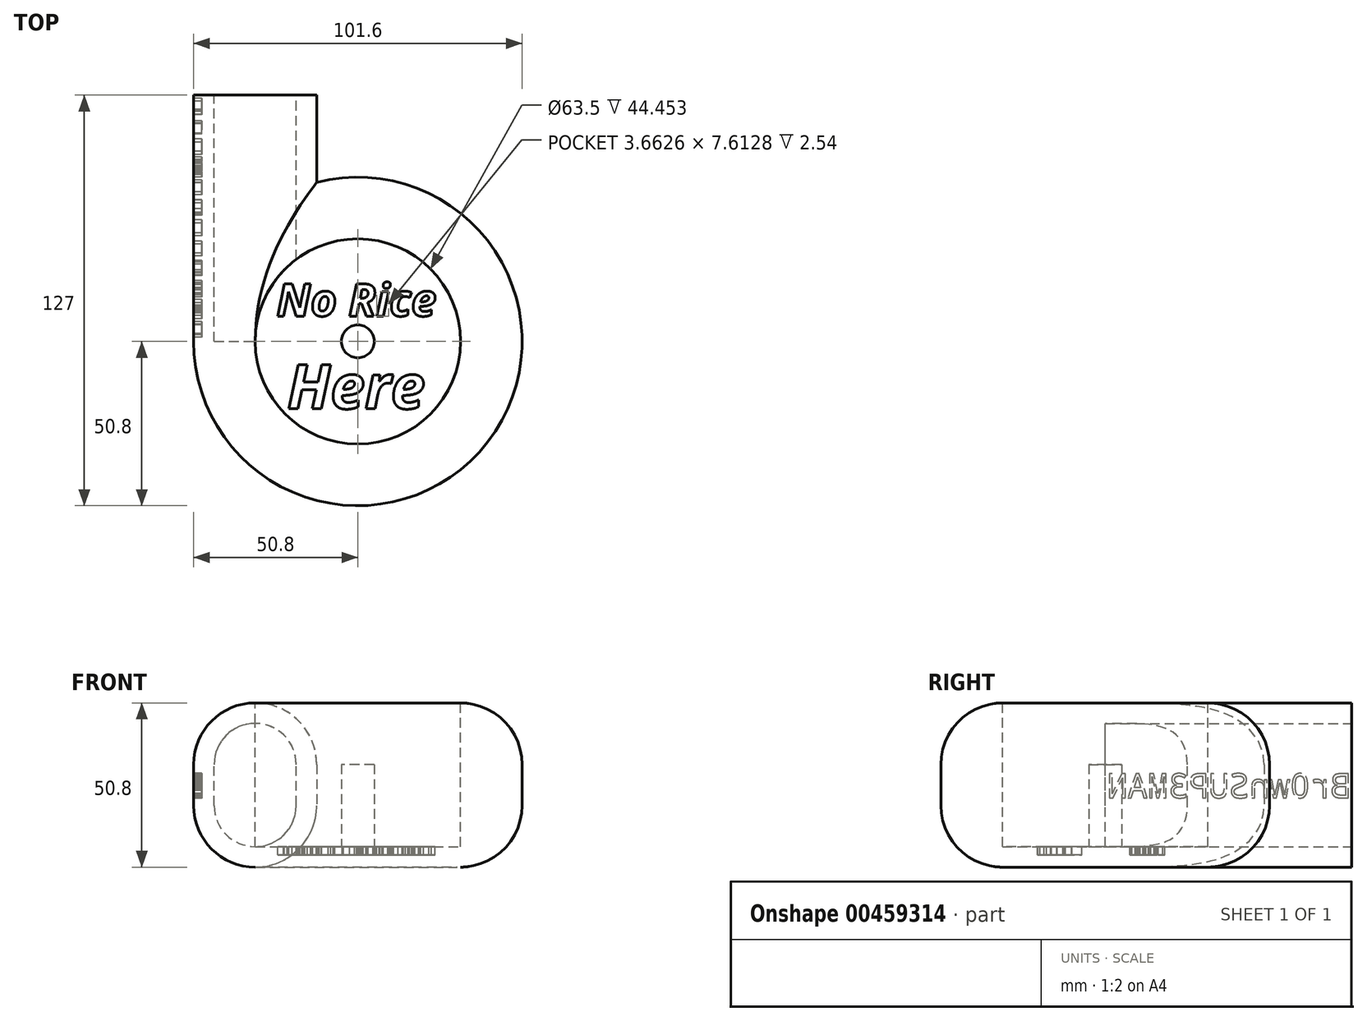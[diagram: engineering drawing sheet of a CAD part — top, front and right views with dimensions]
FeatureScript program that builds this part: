
annotation { "Feature Type Name" : "Feature", "Feature Type Description" : "" }
export const myFeature = defineFeature(function(context is Context, id is Id, definition is map)
    precondition{}
    {
        {
            var Q0;
            Q0=qCreatedBy(makeId("Top.planeOp"),FACE);
            var sketch = newSketch(context, id + "F0", { "sketchPlane" : qUnion([Q0])});
            skLineSegment(sketch, "E0", {"start": v(-50.8, 0) * mm, "end": v(-50.8, 76.2) * mm});
            skLineSegment(sketch, "E1", {"start": v(-50.8, 76.2) * mm, "end": v(-12.7, 76.2) * mm});
            skLineSegment(sketch, "E2", {"start": v(-12.7, 76.2) * mm, "end": v(-12.7, 49.19) * mm});
            skArc(sketch, "E3", {"start": v(-50.8, 0) * mm, "mid": v(40.16, -31.1) * mm, "end": v(-12.7, 49.19) * mm});
            skSolve(sketch);
        }
        {
            var Q0;
            Q0=makeQuery(id+"F0.imprint","IMPRINT",FACE,{"disambiguationData":[TD([[makeQuery(id+"F0.imprint","IMPRINT",EDGE,{"derivedFrom":sQuery(id+"F0.wireOp",EDGE,"E0")}),-1.0]])]});
            extrude(context, id + "F1", {"entities" : qUnion([Q0]), "depth" : 50.8 * mm});
        }
        {
            var Q0;
            Q0=makeQuery(id+"F1.opExtrude","CAP_EDGE",EDGE,{"disambiguationData":[OSD([sQuery(id+"F0.wireOp",EDGE,"E0")])],"isStart":false});
            var Q1;
            Q1=makeQuery(id+"F1.opExtrude","CAP_EDGE",EDGE,{"disambiguationData":[OSD([sQuery(id+"F0.wireOp",EDGE,"E2")])],"isStart":false});
            fillet(context, id + "F2", {"entities" : qUnion([Q0, Q1]), "radius" : 19.05 * mm, "tangentPropagation" : true, "allowEdgeOverflow" : false});
        }
        {
            var Q0;
            Q0=makeQuery(id+"F1.opExtrude","CAP_EDGE",EDGE,{"disambiguationData":[OSD([sQuery(id+"F0.wireOp",EDGE,"E0")])],"isStart":true});
            var Q1;
            Q1=makeQuery(id+"F1.opExtrude","CAP_EDGE",EDGE,{"disambiguationData":[OSD([sQuery(id+"F0.wireOp",EDGE,"E2")])],"isStart":true});
            fillet(context, id + "F3", {"entities" : qUnion([Q0, Q1]), "radius" : 19.05 * mm, "tangentPropagation" : true, "allowEdgeOverflow" : false});
        }
        {
            var Q0;
            Q0=makeQuery(id+"F1.opExtrude","SWEPT_FACE",FACE,{"disambiguationData":[OSD([sQuery(id+"F0.wireOp",EDGE,"E1")])]});
            var sketch = newSketch(context, id + "F4", { "sketchPlane" : qUnion([Q0])});
            skLineSegment(sketch, "E4", {"start": v(44.45, 6.35) * mm, "end": v(19.05, 6.35) * mm});
            skLineSegment(sketch, "E5", {"start": v(44.45, 44.45) * mm, "end": v(44.45, 44.45) * mm});
            skLineSegment(sketch, "E6", {"start": v(44.45, 6.35) * mm, "end": v(44.45, 44.45) * mm});
            skLineSegment(sketch, "E7", {"start": v(19.05, 6.35) * mm, "end": v(19.05, 6.35) * mm});
            skLineSegment(sketch, "E8", {"start": v(19.05, 6.35) * mm, "end": v(19.05, 44.45) * mm});
            skLineSegment(sketch, "E9", {"start": v(44.45, 44.45) * mm, "end": v(19.05, 44.45) * mm});
            skSolve(sketch);
        }
        {
            var Q0;
            Q0=makeQuery(id+"F4.imprint","IMPRINT",FACE,{"disambiguationData":[TD([[makeQuery(id+"F4.imprint","IMPRINT",EDGE,{"derivedFrom":sQuery(id+"F4.wireOp",EDGE,"E4")}),-1.0]])]});
            extrude(context, id + "F5", {"entities" : qUnion([Q0]), "operationType" : NewBodyOperationType.ADD, "depth" : 25.4 * mm});
        }
        {
            var Q0;
            Q0=makeQuery(id+"F5.opExtrude","SWEPT_EDGE",EDGE,{"disambiguationData":[OSD([sQuery(id+"F4.wireOp",EDGE,"E4"),sQuery(id+"F4.wireOp",EDGE,"E6")])]});
            var Q1;
            Q1=makeQuery(id+"F5.opExtrude","SWEPT_EDGE",EDGE,{"disambiguationData":[OSD([sQuery(id+"F4.wireOp",EDGE,"E4"),sQuery(id+"F4.wireOp",EDGE,"E8")])]});
            var Q2;
            Q2=makeQuery(id+"F5.opExtrude","SWEPT_EDGE",EDGE,{"disambiguationData":[OSD([sQuery(id+"F4.wireOp",EDGE,"E8"),sQuery(id+"F4.wireOp",EDGE,"E9")])]});
            var Q3;
            Q3=makeQuery(id+"F5.opExtrude","SWEPT_EDGE",EDGE,{"disambiguationData":[OSD([sQuery(id+"F4.wireOp",EDGE,"E6"),sQuery(id+"F4.wireOp",EDGE,"E9")])]});
            fillet(context, id + "F6", {"entities" : qUnion([Q0, Q1, Q2, Q3]), "radius" : 12.7 * mm, "tangentPropagation" : true, "allowEdgeOverflow" : false});
        }
        {
            var Q0;
            Q0=makeQuery(id+"F5.opExtrude","CAP_FACE",FACE,{"disambiguationData":[OSD([sQuery(id+"F4.wireOp",EDGE,"E4"),sQuery(id+"F4.wireOp",EDGE,"E6"),sQuery(id+"F4.wireOp",EDGE,"E8"),sQuery(id+"F4.wireOp",EDGE,"E9")])],"isStart":false});
            extrude(context, id + "F7", {"entities" : qUnion([Q0]), "operationType" : NewBodyOperationType.REMOVE, "oppositeDirection" : true, "depth" : 101.6 * mm});
        }
        {
            var Q0;
            Q0=makeQuery(id+"F1.opExtrude","CAP_FACE",FACE,{"disambiguationData":[OSD([sQuery(id+"F0.wireOp",EDGE,"E0"),sQuery(id+"F0.wireOp",EDGE,"E1"),sQuery(id+"F0.wireOp",EDGE,"E2"),sQuery(id+"F0.wireOp",EDGE,"E3")])],"isStart":false});
            extrude(context, id + "F8", {"entities" : qUnion([Q0]), "operationType" : NewBodyOperationType.REMOVE, "oppositeDirection" : true, "depth" : 44.45 * mm});
        }
        {
            var Q0;
            Q0=makeQuery(id+"F8.boolean.opBoolean","COPY",FACE,{"derivedFrom":makeQuery(id+"F8.opExtrude","CAP_FACE",FACE,{"disambiguationData":[OSD([sQuery(id+"F0.wireOp",EDGE,"E0"),sQuery(id+"F0.wireOp",EDGE,"E1"),sQuery(id+"F0.wireOp",EDGE,"E2"),sQuery(id+"F0.wireOp",EDGE,"E3")])],"isStart":false})});
            var sketch = newSketch(context, id + "F9", { "sketchPlane" : qUnion([Q0])});
            skCircle(sketch, "E10", {"center": v(0, 0) * mm, "radius": 5.08 * mm});
            skSolve(sketch);
        }
        {
            var Q0;
            Q0=makeQuery(id+"F9.imprint","IMPRINT",FACE,{"disambiguationData":[TD([[makeQuery(id+"F9.imprint","IMPRINT",EDGE,{"derivedFrom":sQuery(id+"F9.wireOp",EDGE,"E10")}),1.0]])]});
            extrude(context, id + "F10", {"entities" : qUnion([Q0]), "operationType" : NewBodyOperationType.ADD, "depth" : 25.4 * mm});
        }
        {
            var Q0;
            Q0=makeQuery(id+"F1.opExtrude","SWEPT_FACE",FACE,{"disambiguationData":[OSD([sQuery(id+"F0.wireOp",EDGE,"E0")])]});
            var sketch = newSketch(context, id + "F11", { "sketchPlane" : qUnion([Q0])});
            skText(sketch, "E11", { "text": "Br0wnSUP3MAN", "fontName": "DroidSansMono.ttf"});
            const initialGuessF11  = {"E11": [-0.07592, 0.02143, 1, 0, 0.00753]};
            skSetInitialGuess(sketch, initialGuessF11);
            skSolve(sketch);
        }
        {
            var Q0;
            Q0 = qSketchRegion(id + "F11", true);
            extrude(context, id + "F12", {"entities" : qUnion([Q0]), "operationType" : NewBodyOperationType.REMOVE, "oppositeDirection" : true, "depth" : 2.54 * mm});
        }
        {
            var Q0;
            Q0=makeQuery(id+"F9.imprint","IMPRINT",FACE,{"disambiguationData":[TD([[makeQuery(id+"F9.imprint","IMPRINT",EDGE,{"derivedFrom":sQuery(id+"F9.wireOp",EDGE,"E10")}),-1.0]])]});
            var sketch = newSketch(context, id + "F13", { "sketchPlane" : qUnion([Q0])});
            skText(sketch, "E12", { "text": "No Rice", "fontName": "OpenSans-BoldItalic.ttf"});
            skText(sketch, "E13", { "text": "Here", "fontName": "OpenSans-BoldItalic.ttf"});
            const initialGuessF13  = {"E12": [-0.02517, 0.00784, 1, 0, 0.01004], "E13": [-0.02182, -0.02081, 1, 0, 0.01372]};
            skSetInitialGuess(sketch, initialGuessF13);
            skSolve(sketch);
        }
        {
            var Q0;
            Q0 = qSketchRegion(id + "F13", true);
            extrude(context, id + "F14", {"entities" : qUnion([Q0]), "operationType" : NewBodyOperationType.REMOVE, "oppositeDirection" : true, "depth" : 2.54 * mm});
        }
    });
